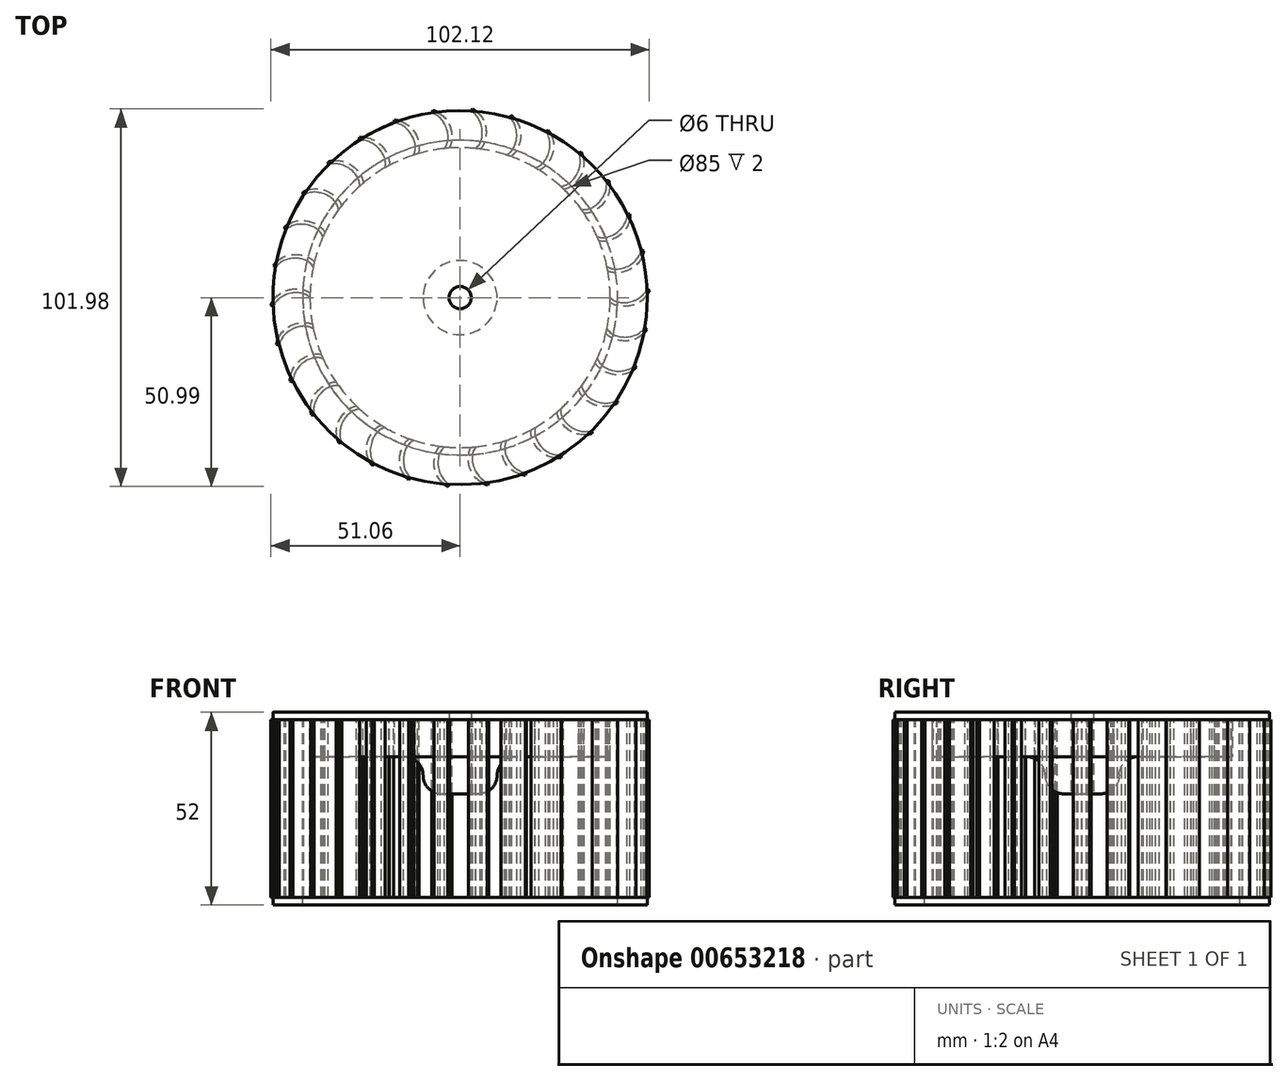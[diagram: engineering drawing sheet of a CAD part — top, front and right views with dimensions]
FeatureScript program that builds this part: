
annotation { "Feature Type Name" : "Feature", "Feature Type Description" : "" }
export const myFeature = defineFeature(function(context is Context, id is Id, definition is map)
    precondition{}
    {
        {
            var Q0;
            Q0=qCreatedBy(makeId("Top.planeOp"),FACE);
            var sketch = newSketch(context, id + "F0", { "sketchPlane" : qUnion([Q0])});
            skCircle(sketch, "E0", {"center": v(0, 0) * mm, "radius": 40.5 * mm});
            skSolve(sketch);
        }
        {
            var Q0;
            Q0=makeQuery(id+"F0.imprint","IMPRINT",FACE,{"disambiguationData":[TD([[makeQuery(id+"F0.imprint","IMPRINT",EDGE,{"derivedFrom":sQuery(id+"F0.wireOp",EDGE,"E0")}),1.0]])]});
            extrude(context, id + "F1", {"entities" : qUnion([Q0]), "depth" : 10 * mm, "offsetDistance" : 25 * mm});
        }
        {
            var Q0;
            Q0=makeQuery(id+"F1.opExtrude","CAP_FACE",FACE,{"disambiguationData":[OSD([sQuery(id+"F0.wireOp",EDGE,"E0")])],"isStart":false});
            var sketch = newSketch(context, id + "F2", { "sketchPlane" : qUnion([Q0])});
            skFitSpline(sketch, "E1", {"points": [v(20.2, 35.1) * mm, v(23.11, 44.9) * mm], "startDerivative": vector(10.47, 2.18) * mm, "endDerivative": vector(-7.52, 9.43) * mm});
            skFitSpline(sketch, "E2", {"points": [v(23.8, 45.21) * mm, v(21.24, 34.49) * mm], "startDerivative": vector(11.47, -15.62) * mm, "endDerivative": vector(-4.9, -0.12) * mm});
            skLineSegment(sketch, "E3", {"start": v(23.11, 44.9) * mm, "end": v(23.8, 45.21) * mm});
            skLineSegment(sketch, "E4", {"start": v(20.2, 35.1) * mm, "end": v(21.24, 34.49) * mm});
            skSolve(sketch);
        }
        {
            var Q0;
            {var subQ0=sQuery(id+"F2.wireOp",EDGE,"E1");Q0=makeQuery(id+"F2.imprint","IMPRINT",FACE,{"disambiguationData":[TD([[makeQuery(id+"F2.imprint","IMPRINT",EDGE,{"derivedFrom":subQ0}),-1.0]])]});}
            extrude(context, id + "F3", {"entities" : qUnion([Q0]), "operationType" : NewBodyOperationType.ADD, "oppositeDirection" : true, "depth" : 48 * mm, "offsetDistance" : 25 * mm});
        }
        {
            var Q0;
            Q0=makeQuery(id+"F1.opExtrude","CAP_FACE",FACE,{"disambiguationData":[OSD([sQuery(id+"F0.wireOp",EDGE,"E0")])],"isStart":true});
            var sketch = newSketch(context, id + "F4", { "sketchPlane" : qUnion([Q0])});
            skCircle(sketch, "E5", {"center": v(0, 0) * mm, "radius": 40 * mm});
            skSolve(sketch);
        }
        {
            var Q0;
            Q0=makeQuery(id+"F1.opExtrude","SWEPT_BODY",BODY,{"disambiguationData":[OSD([sQuery(id+"F0.wireOp",EDGE,"E0")])]});
            var Q1;
            Q1=makeQuery(id+"F1.opExtrude","SWEPT_FACE",FACE,{"disambiguationData":[OSD([sQuery(id+"F0.wireOp",EDGE,"E0")])]});
            circularPattern(context, id + "F5", {"entities" : qUnion([Q0]), "axis" : qUnion([Q1]), "angle" : 360 * degree, "instanceCount" : 30, "equalSpace" : true});
        }
        {
            var Q0;
            {var subQ0=sQuery(id+"F0.wireOp",EDGE,"E0");Q0=makeQuery(id+"F3.boolean.opBoolean","MERGE",FACE,{"derivedFrom":[makeQuery(id+"F1.opExtrude","CAP_FACE",FACE,{"disambiguationData":[OSD([subQ0])],"isStart":false}),makeQuery(id+"F3.opExtrude","CAP_FACE",FACE,{"disambiguationData":[OSD([subQ0,sQuery(id+"F2.wireOp",EDGE,"E1"),sQuery(id+"F2.wireOp",EDGE,"E2"),sQuery(id+"F2.wireOp",EDGE,"E3")])],"isStart":true})]});}
            var sketch = newSketch(context, id + "F6", { "sketchPlane" : qUnion([Q0])});
            skCircle(sketch, "E6", {"center": v(0, 0) * mm, "radius": 50.5 * mm});
            skSolve(sketch);
        }
        {
            var Q0;
            Q0 = qSketchRegion(id + "F6", true);
            extrude(context, id + "F7", {"entities" : qUnion([Q0]), "operationType" : NewBodyOperationType.ADD, "depth" : 2 * mm, "offsetDistance" : 25 * mm});
        }
        {
            var Q0;
            Q0=makeQuery(id+"F5.opPattern","COPY",FACE,{"derivedFrom":makeQuery(id+"F3.opExtrude","CAP_FACE",FACE,{"disambiguationData":[OSD([sQuery(id+"F0.wireOp",EDGE,"E0"),sQuery(id+"F2.wireOp",EDGE,"E1"),sQuery(id+"F2.wireOp",EDGE,"E2"),sQuery(id+"F2.wireOp",EDGE,"E3")])],"isStart":false}),"instanceName":"15"});
            var sketch = newSketch(context, id + "F8", { "sketchPlane" : qUnion([Q0])});
            skCircle(sketch, "E7", {"center": v(0, 0) * mm, "radius": 50.5 * mm});
            skCircle(sketch, "E8", {"center": v(0, 0) * mm, "radius": 42.5 * mm});
            skSolve(sketch);
        }
        {
            var Q0;
            Q0 = qSketchRegion(id + "F8", true);
            extrude(context, id + "F9", {"entities" : qUnion([Q0]), "depth" : 2 * mm, "offsetDistance" : 25 * mm});
        }
        {
            var Q0;
            Q0=makeQuery(id+"F4.imprint","IMPRINT",FACE,{"disambiguationData":[TD([[makeQuery(id+"F4.imprint","IMPRINT",EDGE,{"derivedFrom":sQuery(id+"F4.wireOp",EDGE,"E5")}),1.0]])]});
            var sketch = newSketch(context, id + "F10", { "sketchPlane" : qUnion([Q0])});
            skCircle(sketch, "E9", {"center": v(0, 0) * mm, "radius": 3 * mm});
            skSolve(sketch);
        }
        {
            var Q0;
            Q0 = qSketchRegion(id + "F10", true);
            extrude(context, id + "F11", {"entities" : qUnion([Q0]), "operationType" : NewBodyOperationType.REMOVE, "oppositeDirection" : true, "depth" : 25 * mm, "offsetDistance" : 25 * mm});
        }
        {
            var Q0;
            Q0=makeQuery(id+"F4.imprint","IMPRINT",FACE,{"disambiguationData":[TD([[makeQuery(id+"F4.imprint","IMPRINT",EDGE,{"derivedFrom":sQuery(id+"F4.wireOp",EDGE,"E5")}),1.0]])]});
            var sketch = newSketch(context, id + "F12", { "sketchPlane" : qUnion([Q0])});
            skCircle(sketch, "E10", {"center": v(0, 0) * mm, "radius": 3 * mm});
            skCircle(sketch, "E11", {"center": v(0, 0) * mm, "radius": 10 * mm});
            skSolve(sketch);
        }
        {
            var Q0;
            Q0 = qSketchRegion(id + "F12", true);
            extrude(context, id + "F13", {"entities" : qUnion([Q0]), "operationType" : NewBodyOperationType.ADD, "depth" : 10 * mm, "offsetDistance" : 25 * mm});
        }
        {
            var Q0;
            Q0=makeQuery(id+"F13.opExtrude","SWEPT_FACE",FACE,{"disambiguationData":[OSD([sQuery(id+"F12.wireOp",EDGE,"E11")])]});
            fillet(context, id + "F14", {"entities" : qUnion([Q0]), "radius" : 5 * mm, "tangentPropagation" : true, "allowEdgeOverflow" : false});
        }
        {
            var Q0;
            Q0 = qSketchRegion(id + "F8", true);
            extrude(context, id + "F15", {"entities" : qUnion([Q0]), "operationType" : NewBodyOperationType.ADD, "depth" : 2 * mm, "offsetDistance" : 25 * mm});
        }
    });
